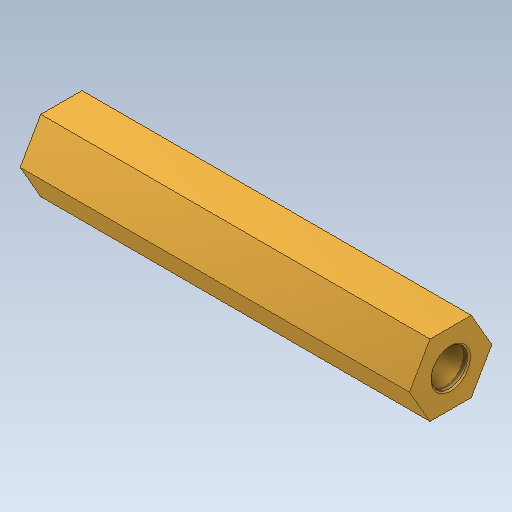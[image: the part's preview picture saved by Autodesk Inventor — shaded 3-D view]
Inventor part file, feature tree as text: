
AUTODESK INVENTOR PART (.ipt)
format: ipt  version: 2021 (Build 250183000, 183)  size: 122,880 bytes
history: native  units: mm
features: other x5, thread x4, chamfer x2, revolve x1
ambient origin geometry x6: Origin, XZ Plane, XY Plane, X Axis, Y Axis, Z Axis
bodies: Solid1 (feature_tree)
feature tree (12):
  revolve  "Revolution1"  [1 undecoded]
  other  "N-Side1"
  thread  "Thread4"  [1 undecoded]
  thread  "Thread2"  [1 undecoded]
  other  "Start Plane"
  other  "Origin point"
  other  "Main Sketch"
  other  "iFeature1:1"
  thread  "Thread1"  [1 undecoded]
  chamfer  "Chamfer1"  [1 undecoded]
  thread  "Thread3"  [1 undecoded]
  chamfer  "Chamfer2"  Distance=0.09mm Angle=45.0deg
note: 6 required parameter values undecoded (feature->parameter linkage not recoverable at this tier; creation-order binding heuristic only, values carry confidence <= 0.55)